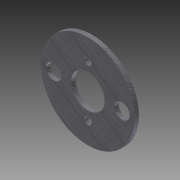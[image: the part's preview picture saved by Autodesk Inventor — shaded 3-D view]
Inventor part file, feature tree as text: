
AUTODESK INVENTOR PART (.ipt)
format: ipt  version: 2012 (Build 160160000, 160)  size: 100,864 bytes
history: native  units: in
note: dims shown in document units (in); Inventor stores cm internally (conversion verified against a paired STEP export)
features: sketch x1, extrude x1, hole x1
ambient origin geometry x8: Origin, YZ Plane, XZ Plane, XY Plane, X Axis, Y Axis, Z Axis, Center Point
bodies: Solid1 (feature_tree)
feature tree (3):
  sketch  "Sketch1"  dims[d0=1.715in d1=0.6125in d2=0.944in d3=0.28in d4=0.28in d5=1.25in d6=0.625in d7=0.078in d8=0.0in d9=0.13in d10=0.75in d11=0.375in d12=0.25in d13=0.5635in d14=1.0in d15=0.8108in]
  extrude  "Extrusion1"  Depth=0.6125in
  hole  "Hole1"  [1 undecoded]
note: 1 required parameter value undecoded (feature->parameter linkage not recoverable at this tier; creation-order binding heuristic only, values carry confidence <= 0.55)
